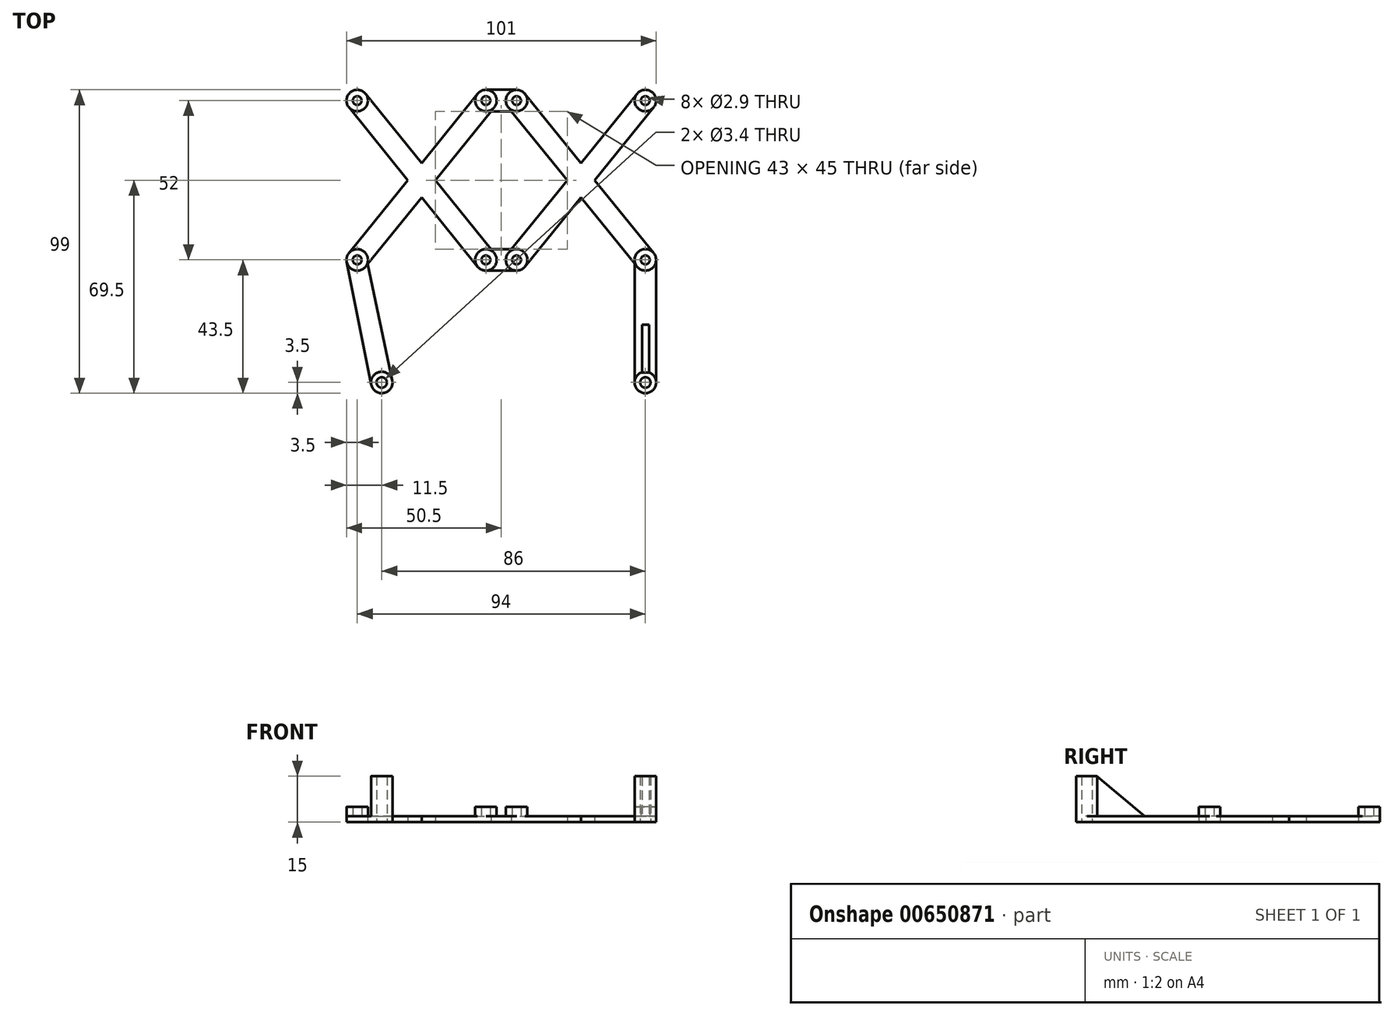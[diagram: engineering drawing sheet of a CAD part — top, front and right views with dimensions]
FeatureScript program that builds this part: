
annotation { "Feature Type Name" : "Feature", "Feature Type Description" : "" }
export const myFeature = defineFeature(function(context is Context, id is Id, definition is map)
    precondition{}
    {
        {
            var Q0;
            Q0=qCreatedBy(makeId("Top.planeOp"),FACE);
            var sketch = newSketch(context, id + "F0", { "sketchPlane" : qUnion([Q0])});
            skCircle(sketch, "E0", {"center": v(0, 0) * mm, "radius": 3.5 * mm});
            skCircle(sketch, "E1", {"center": v(42, 0) * mm, "radius": 3.5 * mm});
            skCircle(sketch, "E2", {"center": v(0, -52) * mm, "radius": 3.5 * mm});
            skCircle(sketch, "E3", {"center": v(42, -52) * mm, "radius": 3.5 * mm});
            skCircle(sketch, "E4", {"center": v(94, -92) * mm, "radius": 3.5 * mm});
            skCircle(sketch, "E5", {"center": v(0, 0) * mm, "radius": 1.45 * mm});
            skCircle(sketch, "E6", {"center": v(42, 0) * mm, "radius": 1.45 * mm});
            skCircle(sketch, "E7", {"center": v(42, -52) * mm, "radius": 1.45 * mm});
            skCircle(sketch, "E8", {"center": v(0, -52) * mm, "radius": 1.45 * mm});
            skCircle(sketch, "E9", {"center": v(94, -92) * mm, "radius": 1.7 * mm});
            skLineSegment(sketch, "E10", {"start": v(-2.72, -2.2) * mm, "end": v(39.28, -54.2) * mm});
            skLineSegment(sketch, "E11", {"start": v(2.72, 2.2) * mm, "end": v(44.72, -49.8) * mm});
            skLineSegment(sketch, "E12", {"start": v(-2.72, -49.8) * mm, "end": v(39.28, 2.2) * mm});
            skLineSegment(sketch, "E13", {"start": v(2.72, -54.2) * mm, "end": v(44.72, -2.2) * mm});
            skPoint(sketch, "E14", {"position": v(8, -92) * mm});
            skCircle(sketch, "E15", {"center": v(8, -92) * mm, "radius": 1.7 * mm});
            skCircle(sketch, "E16", {"center": v(8, -92) * mm, "radius": 3.5 * mm});
            skLineSegment(sketch, "E17", {"start": v(-3.43, -52.69) * mm, "end": v(4.57, -92.69) * mm});
            skLineSegment(sketch, "E18", {"start": v(2.72, -49.8) * mm, "end": v(11.43, -91.28) * mm});
            skPoint(sketch, "E19", {"position": v(52, -52) * mm});
            skCircle(sketch, "E20", {"center": v(52, -52) * mm, "radius": 1.45 * mm});
            skCircle(sketch, "E21", {"center": v(52, -52) * mm, "radius": 3.5 * mm});
            skPoint(sketch, "E22", {"position": v(94, -52) * mm});
            skCircle(sketch, "E23", {"center": v(94, -52) * mm, "radius": 1.45 * mm});
            skCircle(sketch, "E24", {"center": v(94, -52) * mm, "radius": 3.5 * mm});
            skPoint(sketch, "E25", {"position": v(52, 0) * mm});
            skPoint(sketch, "E26", {"position": v(94, 0) * mm});
            skCircle(sketch, "E27", {"center": v(52, 0) * mm, "radius": 1.45 * mm});
            skCircle(sketch, "E28", {"center": v(52, 0) * mm, "radius": 3.5 * mm});
            skCircle(sketch, "E29", {"center": v(94, 0) * mm, "radius": 1.45 * mm});
            skCircle(sketch, "E30", {"center": v(94, 0) * mm, "radius": 3.5 * mm});
            skLineSegment(sketch, "E31", {"start": v(49.28, -49.8) * mm, "end": v(91.28, 2.2) * mm});
            skLineSegment(sketch, "E32", {"start": v(96.72, -2.2) * mm, "end": v(54.72, -54.2) * mm});
            skLineSegment(sketch, "E33", {"start": v(49.28, -2.2) * mm, "end": v(91.28, -54.2) * mm});
            skLineSegment(sketch, "E34", {"start": v(54.72, 2.2) * mm, "end": v(96.72, -49.8) * mm});
            skLineSegment(sketch, "E35", {"start": v(42, -55.5) * mm, "end": v(52, -55.5) * mm});
            skLineSegment(sketch, "E36", {"start": v(42, -48.5) * mm, "end": v(52, -48.5) * mm});
            skLineSegment(sketch, "E37", {"start": v(42, -3.5) * mm, "end": v(52, -3.5) * mm});
            skLineSegment(sketch, "E38", {"start": v(42, 3.5) * mm, "end": v(52, 3.5) * mm});
            skLineSegment(sketch, "E39", {"start": v(90.5, -92) * mm, "end": v(90.5, -52) * mm});
            skLineSegment(sketch, "E40", {"start": v(97.5, -52) * mm, "end": v(97.5, -92) * mm});
            skSolve(sketch);
        }
        {
            var Q0;
            {var subQ1=sQuery(id+"F0.wireOp",EDGE,"E2");var subQ5=sQuery(id+"F0.wireOp",EDGE,"E18");var subQ6=makeQuery(id+"F0.imprint","INTERSECT",VERTEX,{"disambiguationData":[OD(0.0)],"derivedFrom":[subQ1,subQ5]});Q0=makeQuery(id+"F0.imprint","IMPRINT",FACE,{"disambiguationData":[TD([[makeQuery(id+"F0.imprint","IMPRINT",EDGE,{"disambiguationData":[TD([[subQ6,1.0]])],"derivedFrom":subQ1}),-1.0]])]});}
            var Q1;
            {var subQ0=sQuery(id+"F0.wireOp",EDGE,"E10");var subQ1=sQuery(id+"F0.wireOp",EDGE,"E0");var subQ2=makeQuery(id+"F0.imprint","INTERSECT",VERTEX,{"derivedFrom":[subQ1,subQ0]});Q1=makeQuery(id+"F0.imprint","IMPRINT",FACE,{"disambiguationData":[TD([[makeQuery(id+"F0.imprint","IMPRINT",EDGE,{"disambiguationData":[TD([[subQ2,-1.0]])],"derivedFrom":subQ1}),-1.0]])]});}
            var Q2;
            {var subQ5=sQuery(id+"F0.wireOp",EDGE,"E12");var subQ6=sQuery(id+"F0.wireOp",EDGE,"E1");var subQ7=makeQuery(id+"F0.imprint","INTERSECT",VERTEX,{"derivedFrom":[subQ6,subQ5]});Q2=makeQuery(id+"F0.imprint","IMPRINT",FACE,{"disambiguationData":[TD([[makeQuery(id+"F0.imprint","IMPRINT",EDGE,{"disambiguationData":[TD([[subQ7,-1.0]])],"derivedFrom":subQ6}),-1.0]])]});}
            var Q3;
            {var subQ0=sQuery(id+"F0.wireOp",EDGE,"E12");var subQ1=sQuery(id+"F0.wireOp",EDGE,"E10");var subQ2=makeQuery(id+"F0.imprint","INTERSECT",VERTEX,{"derivedFrom":[subQ1,subQ0]});Q3=makeQuery(id+"F0.imprint","IMPRINT",FACE,{"disambiguationData":[TD([[makeQuery(id+"F0.imprint","IMPRINT",EDGE,{"disambiguationData":[TD([[subQ2,-1.0]])],"derivedFrom":subQ1}),1.0]])]});}
            var Q4;
            {var subQ1=sQuery(id+"F0.wireOp",EDGE,"E10");var subQ5=sQuery(id+"F0.wireOp",EDGE,"E3");var subQ6=makeQuery(id+"F0.imprint","INTERSECT",VERTEX,{"derivedFrom":[subQ5,subQ1]});Q4=makeQuery(id+"F0.imprint","IMPRINT",FACE,{"disambiguationData":[TD([[makeQuery(id+"F0.imprint","IMPRINT",EDGE,{"disambiguationData":[TD([[subQ6,1.0]])],"derivedFrom":subQ5}),-1.0]])]});}
            var Q5;
            {var subQ5=sQuery(id+"F0.wireOp",EDGE,"E35");Q5=makeQuery(id+"F0.imprint","IMPRINT",FACE,{"disambiguationData":[TD([[makeQuery(id+"F0.imprint","IMPRINT",EDGE,{"derivedFrom":subQ5}),1.0]])]});}
            var Q6;
            {var subQ0=sQuery(id+"F0.wireOp",EDGE,"E17");Q6=makeQuery(id+"F0.imprint","IMPRINT",FACE,{"disambiguationData":[TD([[makeQuery(id+"F0.imprint","IMPRINT",EDGE,{"derivedFrom":subQ0}),1.0]])]});}
            var Q7;
            {var subQ1=sQuery(id+"F0.wireOp",EDGE,"E32");var subQ5=sQuery(id+"F0.wireOp",EDGE,"E21");var subQ6=makeQuery(id+"F0.imprint","INTERSECT",VERTEX,{"derivedFrom":[subQ5,subQ1]});Q7=makeQuery(id+"F0.imprint","IMPRINT",FACE,{"disambiguationData":[TD([[makeQuery(id+"F0.imprint","IMPRINT",EDGE,{"disambiguationData":[TD([[subQ6,-1.0]])],"derivedFrom":subQ5}),-1.0]])]});}
            var Q8;
            {var subQ5=sQuery(id+"F0.wireOp",EDGE,"E34");var subQ6=sQuery(id+"F0.wireOp",EDGE,"E28");var subQ7=makeQuery(id+"F0.imprint","INTERSECT",VERTEX,{"derivedFrom":[subQ6,subQ5]});Q8=makeQuery(id+"F0.imprint","IMPRINT",FACE,{"disambiguationData":[TD([[makeQuery(id+"F0.imprint","IMPRINT",EDGE,{"disambiguationData":[TD([[subQ7,1.0]])],"derivedFrom":subQ6}),-1.0]])]});}
            var Q9;
            {var subQ9=sQuery(id+"F0.wireOp",EDGE,"E38");Q9=makeQuery(id+"F0.imprint","IMPRINT",FACE,{"disambiguationData":[TD([[makeQuery(id+"F0.imprint","IMPRINT",EDGE,{"derivedFrom":subQ9}),-1.0]])]});}
            var Q10;
            {var subQ0=sQuery(id+"F0.wireOp",EDGE,"E34");var subQ1=sQuery(id+"F0.wireOp",EDGE,"E31");var subQ2=makeQuery(id+"F0.imprint","INTERSECT",VERTEX,{"derivedFrom":[subQ1,subQ0]});Q10=makeQuery(id+"F0.imprint","IMPRINT",FACE,{"disambiguationData":[TD([[makeQuery(id+"F0.imprint","IMPRINT",EDGE,{"disambiguationData":[TD([[subQ2,1.0]])],"derivedFrom":subQ1}),-1.0]])]});}
            var Q11;
            {var subQ0=sQuery(id+"F0.wireOp",EDGE,"E31");var subQ1=sQuery(id+"F0.wireOp",EDGE,"E30");var subQ2=makeQuery(id+"F0.imprint","INTERSECT",VERTEX,{"derivedFrom":[subQ1,subQ0]});Q11=makeQuery(id+"F0.imprint","IMPRINT",FACE,{"disambiguationData":[TD([[makeQuery(id+"F0.imprint","IMPRINT",EDGE,{"disambiguationData":[TD([[subQ2,-1.0]])],"derivedFrom":subQ1}),-1.0]])]});}
            var Q12;
            {var subQ5=sQuery(id+"F0.wireOp",EDGE,"E34");var subQ7=sQuery(id+"F0.wireOp",EDGE,"E24");var subQ8=makeQuery(id+"F0.imprint","INTERSECT",VERTEX,{"derivedFrom":[subQ7,subQ5]});Q12=makeQuery(id+"F0.imprint","IMPRINT",FACE,{"disambiguationData":[TD([[makeQuery(id+"F0.imprint","IMPRINT",EDGE,{"disambiguationData":[TD([[subQ8,-1.0]])],"derivedFrom":subQ7}),-1.0]])]});}
            var Q13;
            {var subQ5=sQuery(id+"F0.wireOp",EDGE,"E40");Q13=makeQuery(id+"F0.imprint","IMPRINT",FACE,{"disambiguationData":[TD([[makeQuery(id+"F0.imprint","IMPRINT",EDGE,{"derivedFrom":subQ5}),-1.0]])]});}
            var Q14;
            Q14=makeQuery(id+"F0.imprint","IMPRINT",FACE,{"disambiguationData":[TD([[makeQuery(id+"F0.imprint","IMPRINT",EDGE,{"derivedFrom":sQuery(id+"F0.wireOp",EDGE,"E5")}),-1.0]])]});
            var Q15;
            Q15=makeQuery(id+"F0.imprint","IMPRINT",FACE,{"disambiguationData":[TD([[makeQuery(id+"F0.imprint","IMPRINT",EDGE,{"derivedFrom":sQuery(id+"F0.wireOp",EDGE,"E6")}),-1.0]])]});
            var Q16;
            Q16=makeQuery(id+"F0.imprint","IMPRINT",FACE,{"disambiguationData":[TD([[makeQuery(id+"F0.imprint","IMPRINT",EDGE,{"derivedFrom":sQuery(id+"F0.wireOp",EDGE,"E27")}),-1.0]])]});
            var Q17;
            Q17=makeQuery(id+"F0.imprint","IMPRINT",FACE,{"disambiguationData":[TD([[makeQuery(id+"F0.imprint","IMPRINT",EDGE,{"derivedFrom":sQuery(id+"F0.wireOp",EDGE,"E29")}),-1.0]])]});
            var Q18;
            Q18=makeQuery(id+"F0.imprint","IMPRINT",FACE,{"disambiguationData":[TD([[makeQuery(id+"F0.imprint","IMPRINT",EDGE,{"derivedFrom":sQuery(id+"F0.wireOp",EDGE,"E23")}),-1.0]])]});
            var Q19;
            Q19=makeQuery(id+"F0.imprint","IMPRINT",FACE,{"disambiguationData":[TD([[makeQuery(id+"F0.imprint","IMPRINT",EDGE,{"derivedFrom":sQuery(id+"F0.wireOp",EDGE,"E9")}),-1.0]])]});
            var Q20;
            Q20=makeQuery(id+"F0.imprint","IMPRINT",FACE,{"disambiguationData":[TD([[makeQuery(id+"F0.imprint","IMPRINT",EDGE,{"derivedFrom":sQuery(id+"F0.wireOp",EDGE,"E20")}),-1.0]])]});
            var Q21;
            Q21=makeQuery(id+"F0.imprint","IMPRINT",FACE,{"disambiguationData":[TD([[makeQuery(id+"F0.imprint","IMPRINT",EDGE,{"derivedFrom":sQuery(id+"F0.wireOp",EDGE,"E7")}),-1.0]])]});
            var Q22;
            Q22=makeQuery(id+"F0.imprint","IMPRINT",FACE,{"disambiguationData":[TD([[makeQuery(id+"F0.imprint","IMPRINT",EDGE,{"derivedFrom":sQuery(id+"F0.wireOp",EDGE,"E15")}),-1.0]])]});
            var Q23;
            {var subQ0=sQuery(id+"F0.wireOp",EDGE,"E13");var subQ1=sQuery(id+"F0.wireOp",EDGE,"E2");var subQ2=makeQuery(id+"F0.imprint","INTERSECT",VERTEX,{"derivedFrom":[subQ1,subQ0]});Q23=makeQuery(id+"F0.imprint","IMPRINT",FACE,{"disambiguationData":[TD([[makeQuery(id+"F0.imprint","IMPRINT",EDGE,{"disambiguationData":[TD([[subQ2,-1.0]])],"derivedFrom":subQ1}),-1.0]])]});}
            var Q24;
            {var subQ0=sQuery(id+"F0.wireOp",EDGE,"E18");var subQ1=sQuery(id+"F0.wireOp",EDGE,"E2");var subQ2=makeQuery(id+"F0.imprint","INTERSECT",VERTEX,{"disambiguationData":[OD(0.0)],"derivedFrom":[subQ1,subQ0]});Q24=makeQuery(id+"F0.imprint","IMPRINT",FACE,{"disambiguationData":[TD([[makeQuery(id+"F0.imprint","IMPRINT",EDGE,{"disambiguationData":[TD([[subQ2,1.0]])],"derivedFrom":subQ1}),1.0]])]});}
            var Q25;
            Q25=makeQuery(id+"F0.imprint","IMPRINT",FACE,{"disambiguationData":[TD([[makeQuery(id+"F0.imprint","IMPRINT",EDGE,{"derivedFrom":sQuery(id+"F0.wireOp",EDGE,"E8")}),-1.0]])]});
            var Q26;
            {var subQ0=sQuery(id+"F0.wireOp",EDGE,"E11");var subQ1=sQuery(id+"F0.wireOp",EDGE,"E3");var subQ2=makeQuery(id+"F0.imprint","INTERSECT",VERTEX,{"derivedFrom":[subQ1,subQ0]});Q26=makeQuery(id+"F0.imprint","IMPRINT",FACE,{"disambiguationData":[TD([[makeQuery(id+"F0.imprint","IMPRINT",EDGE,{"disambiguationData":[TD([[subQ2,-1.0]])],"derivedFrom":subQ1}),-1.0]])]});}
            var Q27;
            {var subQ0=sQuery(id+"F0.wireOp",EDGE,"E31");var subQ1=sQuery(id+"F0.wireOp",EDGE,"E21");var subQ2=makeQuery(id+"F0.imprint","INTERSECT",VERTEX,{"derivedFrom":[subQ1,subQ0]});Q27=makeQuery(id+"F0.imprint","IMPRINT",FACE,{"disambiguationData":[TD([[makeQuery(id+"F0.imprint","IMPRINT",EDGE,{"disambiguationData":[TD([[subQ2,1.0]])],"derivedFrom":subQ1}),-1.0]])]});}
            var Q28;
            {var subQ0=sQuery(id+"F0.wireOp",EDGE,"E13");var subQ1=sQuery(id+"F0.wireOp",EDGE,"E1");var subQ2=makeQuery(id+"F0.imprint","INTERSECT",VERTEX,{"derivedFrom":[subQ1,subQ0]});Q28=makeQuery(id+"F0.imprint","IMPRINT",FACE,{"disambiguationData":[TD([[makeQuery(id+"F0.imprint","IMPRINT",EDGE,{"disambiguationData":[TD([[subQ2,1.0]])],"derivedFrom":subQ1}),-1.0]])]});}
            var Q29;
            {var subQ0=sQuery(id+"F0.wireOp",EDGE,"E33");var subQ1=sQuery(id+"F0.wireOp",EDGE,"E28");var subQ2=makeQuery(id+"F0.imprint","INTERSECT",VERTEX,{"derivedFrom":[subQ1,subQ0]});Q29=makeQuery(id+"F0.imprint","IMPRINT",FACE,{"disambiguationData":[TD([[makeQuery(id+"F0.imprint","IMPRINT",EDGE,{"disambiguationData":[TD([[subQ2,-1.0]])],"derivedFrom":subQ1}),-1.0]])]});}
            var Q30;
            {var subQ0=sQuery(id+"F0.wireOp",EDGE,"E33");var subQ1=sQuery(id+"F0.wireOp",EDGE,"E24");var subQ2=makeQuery(id+"F0.imprint","INTERSECT",VERTEX,{"derivedFrom":[subQ1,subQ0]});Q30=makeQuery(id+"F0.imprint","IMPRINT",FACE,{"disambiguationData":[TD([[makeQuery(id+"F0.imprint","IMPRINT",EDGE,{"disambiguationData":[TD([[subQ2,1.0]])],"derivedFrom":subQ1}),-1.0]])]});}
            extrude(context, id + "F1", {"entities" : qUnion([Q0, Q1, Q2, Q3, Q4, Q5, Q6, Q7, Q8, Q9, Q10, Q11, Q12, Q13, Q14, Q15, Q16, Q17, Q18, Q19, Q20, Q21, Q22, Q23, Q24, Q25, Q26, Q27, Q28, Q29, Q30]), "depth" : 2 * mm, "offsetDistance" : 25 * mm});
        }
        {
            var Q0;
            Q0=makeQuery(id+"F1.opExtrude","CAP_FACE",FACE,{"disambiguationData":[OSD([sQuery(id+"F0.wireOp",EDGE,"E0"),sQuery(id+"F0.wireOp",EDGE,"E1"),sQuery(id+"F0.wireOp",EDGE,"E2"),sQuery(id+"F0.wireOp",EDGE,"QPZae5go-lSce-OIF8-DTbl-BN32yMXIO9b9"),sQuery(id+"F0.wireOp",EDGE,"E3"),sQuery(id+"F0.wireOp",EDGE,"E4"),sQuery(id+"F0.wireOp",EDGE,"E5"),sQuery(id+"F0.wireOp",EDGE,"E6"),sQuery(id+"F0.wireOp",EDGE,"E7"),sQuery(id+"F0.wireOp",EDGE,"E8"),sQuery(id+"F0.wireOp",EDGE,"zt4s2prH-UCs4-EZrs-mIZW-jKnTsjxiMAMK"),sQuery(id+"F0.wireOp",EDGE,"E9"),sQuery(id+"F0.wireOp",EDGE,"E10"),sQuery(id+"F0.wireOp",EDGE,"E11"),sQuery(id+"F0.wireOp",EDGE,"E12"),sQuery(id+"F0.wireOp",EDGE,"E13"),sQuery(id+"F0.wireOp",EDGE,"Jwb00v21-tSXu-5Nsu-5gsD-ivJQaBj8cfK6"),sQuery(id+"F0.wireOp",EDGE,"IYU7JCjG-G5ju-olAL-8J1B-ZKSBjdIHCuS5"),sQuery(id+"F0.wireOp",EDGE,"aur24bt3-EVaU-44Te-4Lnr-yIXF6Gl9pxAS"),sQuery(id+"F0.wireOp",EDGE,"gvncpSO0-wusi-lUM5-SIvC-AsL8Wdbkveul")])],"isStart":false});
            var sketch = newSketch(context, id + "F2", { "sketchPlane" : qUnion([Q0])});
            skCircle(sketch, "E41", {"center": v(0, 0) * mm, "radius": 3.5 * mm});
            skCircle(sketch, "E42", {"center": v(0, 0) * mm, "radius": 1.45 * mm});
            skCircle(sketch, "E43", {"center": v(42, 0) * mm, "radius": 3.5 * mm});
            skCircle(sketch, "E44", {"center": v(42, 0) * mm, "radius": 1.45 * mm});
            skCircle(sketch, "E45", {"center": v(42, -52) * mm, "radius": 3.5 * mm});
            skCircle(sketch, "E46", {"center": v(42, -52) * mm, "radius": 1.45 * mm});
            skCircle(sketch, "E47", {"center": v(0, -52) * mm, "radius": 3.5 * mm});
            skCircle(sketch, "E48", {"center": v(0, -52) * mm, "radius": 1.45 * mm});
            skCircle(sketch, "E49", {"center": v(52, 0) * mm, "radius": 1.45 * mm});
            skCircle(sketch, "E50", {"center": v(52, 0) * mm, "radius": 3.5 * mm});
            skCircle(sketch, "E51", {"center": v(94, 0) * mm, "radius": 1.45 * mm});
            skCircle(sketch, "E52", {"center": v(94, 0) * mm, "radius": 3.5 * mm});
            skCircle(sketch, "E53", {"center": v(94, -52) * mm, "radius": 1.45 * mm});
            skCircle(sketch, "E54", {"center": v(94, -52) * mm, "radius": 3.5 * mm});
            skCircle(sketch, "E55", {"center": v(52, -52) * mm, "radius": 1.45 * mm});
            skCircle(sketch, "E56", {"center": v(52, -52) * mm, "radius": 3.5 * mm});
            skSolve(sketch);
        }
        {
            var Q0;
            Q0 = qSketchRegion(id + "F2", true);
            extrude(context, id + "F3", {"entities" : qUnion([Q0]), "operationType" : NewBodyOperationType.ADD, "depth" : 3 * mm, "offsetDistance" : 25 * mm});
        }
        {
            var Q0;
            Q0=makeQuery(id+"F1.opExtrude","CAP_FACE",FACE,{"disambiguationData":[OSD([sQuery(id+"F0.wireOp",EDGE,"E0"),sQuery(id+"F0.wireOp",EDGE,"E1"),sQuery(id+"F0.wireOp",EDGE,"E2"),sQuery(id+"F0.wireOp",EDGE,"QPZae5go-lSce-OIF8-DTbl-BN32yMXIO9b9"),sQuery(id+"F0.wireOp",EDGE,"E3"),sQuery(id+"F0.wireOp",EDGE,"E4"),sQuery(id+"F0.wireOp",EDGE,"E5"),sQuery(id+"F0.wireOp",EDGE,"E6"),sQuery(id+"F0.wireOp",EDGE,"E7"),sQuery(id+"F0.wireOp",EDGE,"E8"),sQuery(id+"F0.wireOp",EDGE,"zt4s2prH-UCs4-EZrs-mIZW-jKnTsjxiMAMK"),sQuery(id+"F0.wireOp",EDGE,"E9"),sQuery(id+"F0.wireOp",EDGE,"E10"),sQuery(id+"F0.wireOp",EDGE,"E11"),sQuery(id+"F0.wireOp",EDGE,"E12"),sQuery(id+"F0.wireOp",EDGE,"E13"),sQuery(id+"F0.wireOp",EDGE,"Jwb00v21-tSXu-5Nsu-5gsD-ivJQaBj8cfK6"),sQuery(id+"F0.wireOp",EDGE,"IYU7JCjG-G5ju-olAL-8J1B-ZKSBjdIHCuS5"),sQuery(id+"F0.wireOp",EDGE,"aur24bt3-EVaU-44Te-4Lnr-yIXF6Gl9pxAS"),sQuery(id+"F0.wireOp",EDGE,"gvncpSO0-wusi-lUM5-SIvC-AsL8Wdbkveul")])],"isStart":false});
            var sketch = newSketch(context, id + "F4", { "sketchPlane" : qUnion([Q0])});
            skCircle(sketch, "E57", {"center": v(8, -92) * mm, "radius": 3.5 * mm});
            skCircle(sketch, "E58", {"center": v(8, -92) * mm, "radius": 1.7 * mm});
            skCircle(sketch, "E59", {"center": v(94, -92) * mm, "radius": 3.5 * mm});
            skCircle(sketch, "E60", {"center": v(94, -92) * mm, "radius": 1.7 * mm});
            skSolve(sketch);
        }
        {
            var Q0;
            Q0 = qSketchRegion(id + "F4", true);
            extrude(context, id + "F5", {"entities" : qUnion([Q0]), "operationType" : NewBodyOperationType.ADD, "depth" : 13 * mm, "offsetDistance" : 25 * mm});
        }
        {
            var Q0;
            {var subQ14=makeQuery(id+"F1.opExtrude","CAP_EDGE",EDGE,{"disambiguationData":[OSD([sQuery(id+"F0.wireOp",EDGE,"E17")])],"isStart":false});Q0=makeQuery(id+"F4.imprint","IMPRINT",FACE,{"disambiguationData":[TD([[makeQuery(id+"F4.imprint","IMPRINT",EDGE,{"derivedFrom":subQ14}),1.0]])]});}
            var sketch = newSketch(context, id + "F6", { "sketchPlane" : qUnion([Q0])});
            skLineSegment(sketch, "E61.bottom", {"start": v(92.96, -88.7) * mm, "end": v(95.17, -88.7) * mm});
            skLineSegment(sketch, "E61.top", {"start": v(92.96, -70.78) * mm, "end": v(95.17, -70.78) * mm});
            skLineSegment(sketch, "E61.left", {"start": v(92.96, -88.7) * mm, "end": v(92.96, -70.78) * mm});
            skLineSegment(sketch, "E61.right", {"start": v(95.17, -88.7) * mm, "end": v(95.17, -70.78) * mm});
            skSolve(sketch);
        }
        {
            var Q0;
            Q0 = qSketchRegion(id + "F6", true);
            extrude(context, id + "F7", {"entities" : qUnion([Q0]), "operationType" : NewBodyOperationType.ADD, "depth" : 13 * mm, "offsetDistance" : 25 * mm});
        }
        {
            var Q0;
            Q0=makeQuery(id+"F7.opExtrude","CAP_EDGE",EDGE,{"disambiguationData":[OSD([sQuery(id+"F6.wireOp",EDGE,"E61.top")])],"isStart":false});
            chamfer(context, id + "F8", {"entities" : qUnion([Q0]), "chamferType" : ChamferType.TWO_OFFSETS, "width1" : 15 * mm, "oppositeDirection" : false, "width2" : 18 * mm, "tangentPropagation" : true});
        }
    });
